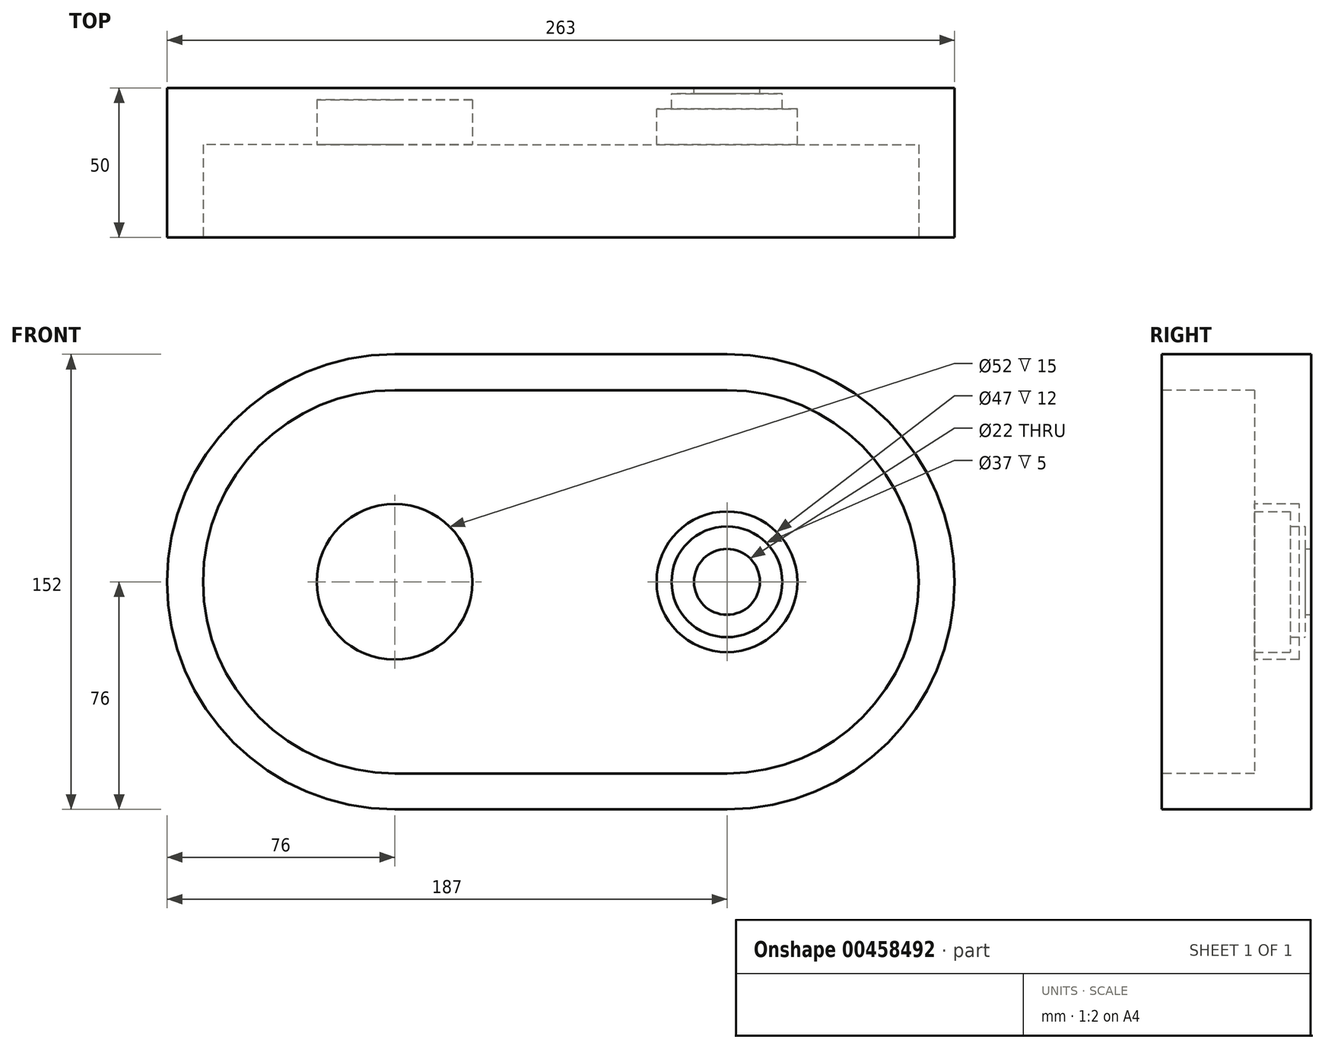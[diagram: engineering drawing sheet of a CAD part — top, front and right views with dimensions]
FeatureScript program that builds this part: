
annotation { "Feature Type Name" : "Feature", "Feature Type Description" : "" }
export const myFeature = defineFeature(function(context is Context, id is Id, definition is map)
    precondition{}
    {
        {
            var Q0;
            Q0=qCreatedBy(makeId("Front.planeOp"),FACE);
            var sketch = newSketch(context, id + "F0", { "sketchPlane" : qUnion([Q0])});
            skArc(sketch, "E0", {"start": v(0, 76) * mm, "mid": v(-69.72, -30.25) * mm, "end": v(55.5, -51.92) * mm});
            skArc(sketch, "E1", {"start": v(55.5, -51.92) * mm, "mid": v(180.72, -30.25) * mm, "end": v(111, 76) * mm});
            skLineSegment(sketch, "E2", {"start": v(111, 0) * mm, "end": v(111, 76) * mm, "construction": true});
            skLineSegment(sketch, "E3", {"start": v(0, 76) * mm, "end": v(111, 76) * mm});
            skLineSegment(sketch, "E4", {"start": v(0, -76) * mm, "end": v(111, -76) * mm});
            skSolve(sketch);
        }
        {
            var Q0;
            Q0 = qSketchRegion(id + "F0", true);
            var Q1;
            {var subQ0=sQuery(id+"F0.wireOp",EDGE,"E3");Q1=makeQuery(id+"F0.imprint","IMPRINT",FACE,{"disambiguationData":[TD([[makeQuery(id+"F0.imprint","IMPRINT",EDGE,{"derivedFrom":subQ0}),-1.0]])]});}
            extrude(context, id + "F1", {"entities" : qUnion([Q0, Q1]), "depth" : 50 * mm});
        }
        {
            var Q0;
            Q0=makeQuery(id+"F1.opExtrude","CAP_FACE",FACE,{"disambiguationData":[OSD([sQuery(id+"F0.wireOp",EDGE,"E0"),sQuery(id+"F0.wireOp",EDGE,"E1"),sQuery(id+"F0.wireOp",EDGE,"E3"),sQuery(id+"F0.wireOp",EDGE,"E4")])],"isStart":false});
            cPlane(context, id + "F2", {"entities" : qUnion([Q0]), "cplaneType" : CPlaneType.OFFSET, "offset" : 0 * mm, "width" : 150 * mm, "height" : 150 * mm});
        }
        {
            var Q0;
            Q0=qCreatedBy(id+"F2.planeOp",FACE);
            var sketch = newSketch(context, id + "F3", { "sketchPlane" : qUnion([Q0])});
            skArc(sketch, "E5", {"start": v(0, 64) * mm, "mid": v(-64, 0) * mm, "end": v(0, -64) * mm});
            skArc(sketch, "E6", {"start": v(111, -64) * mm, "mid": v(175, 0) * mm, "end": v(111, 64) * mm});
            skLineSegment(sketch, "E7", {"start": v(0, 64) * mm, "end": v(111, 64) * mm});
            skLineSegment(sketch, "E8", {"start": v(0, -64) * mm, "end": v(111, -64) * mm});
            skSolve(sketch);
        }
        {
            var Q0;
            Q0 = qSketchRegion(id + "F3", true);
            var Q1;
            Q1=makeQuery(id+"F3.imprint","IMPRINT",FACE,{"disambiguationData":[TD([[makeQuery(id+"F3.imprint","IMPRINT",EDGE,{"derivedFrom":sQuery(id+"F3.wireOp",EDGE,"E5")}),1.0]])]});
            extrude(context, id + "F4", {"entities" : qUnion([Q0, Q1]), "operationType" : NewBodyOperationType.REMOVE, "oppositeDirection" : true, "depth" : 31 * mm});
        }
        {
            var Q0;
            Q0=makeQuery(id+"F4.boolean.opBoolean","COPY",FACE,{"derivedFrom":makeQuery(id+"F4.opExtrude","CAP_FACE",FACE,{"disambiguationData":[OSD([sQuery(id+"F3.wireOp",EDGE,"E5"),sQuery(id+"F3.wireOp",EDGE,"E6"),sQuery(id+"F3.wireOp",EDGE,"E7"),sQuery(id+"F3.wireOp",EDGE,"E8")])],"isStart":false})});
            var sketch = newSketch(context, id + "F5", { "sketchPlane" : qUnion([Q0])});
            skCircle(sketch, "E9", {"center": v(0, 0) * mm, "radius": 26 * mm});
            skSolve(sketch);
        }
        {
            var Q0;
            Q0=makeQuery(id+"F5.imprint","IMPRINT",FACE,{"disambiguationData":[TD([[makeQuery(id+"F5.imprint","IMPRINT",EDGE,{"derivedFrom":sQuery(id+"F5.wireOp",EDGE,"E9")}),1.0]])]});
            extrude(context, id + "F6", {"entities" : qUnion([Q0]), "operationType" : NewBodyOperationType.REMOVE, "oppositeDirection" : true, "depth" : 15 * mm});
        }
        {
            var Q0;
            Q0=qCreatedBy(makeId("Right.planeOp"),FACE);
            cPlane(context, id + "F7", {"entities" : qUnion([Q0]), "cplaneType" : CPlaneType.OFFSET, "offset" : 111 * mm, "width" : 150 * mm, "height" : 150 * mm});
        }
        {
            var Q0;
            Q0=qCreatedBy(id+"F7.planeOp",FACE);
            var sketch = newSketch(context, id + "F8", { "sketchPlane" : qUnion([Q0])});
            skPoint(sketch, "E10.start.orphan", {"position": v(-19, 0) * mm});
            skLineSegment(sketch, "E11", {"start": v(-19, 23.5) * mm, "end": v(-19, 0) * mm});
            skLineSegment(sketch, "E12", {"start": v(0, 0) * mm, "end": v(-19, 0) * mm});
            skLineSegment(sketch, "E13", {"start": v(0, 11) * mm, "end": v(0, 0) * mm});
            skLineSegment(sketch, "E14", {"start": v(-2, 11) * mm, "end": v(0, 11) * mm});
            skLineSegment(sketch, "E15", {"start": v(-2, 18.5) * mm, "end": v(-2, 11) * mm});
            skLineSegment(sketch, "E16", {"start": v(-7, 18.5) * mm, "end": v(-2, 18.5) * mm});
            skLineSegment(sketch, "E17", {"start": v(-7, 23.5) * mm, "end": v(-7, 18.5) * mm});
            skLineSegment(sketch, "E18", {"start": v(-19, 23.5) * mm, "end": v(-7, 23.5) * mm});
            skLineSegment(sketch, "E19", {"start": v(-19, 0) * mm, "end": v(-42.5, 0) * mm, "construction": true});
            skLineSegment(sketch, "E20", {"start": v(-42.5, 0) * mm, "end": v(10.3, 0) * mm, "construction": true});
            skSolve(sketch);
        }
        {
            var Q0;
            Q0 = qSketchRegion(id + "F8", true);
            var Q1;
            Q1=sQuery(id+"F8.wireOp",EDGE,"E20");
            revolve(context, id + "F9", {"operationType" : NewBodyOperationType.REMOVE, "entities" : qUnion([Q0]), "axis" : qUnion([Q1]), "revolveType" : RevolveType.FULL, "oppositeDirection" : true});
        }
    });
